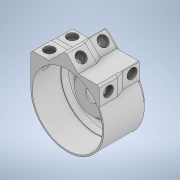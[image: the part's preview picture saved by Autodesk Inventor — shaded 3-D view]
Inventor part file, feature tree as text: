
AUTODESK INVENTOR PART (.ipt)
format: ipt  version: 2021 (Build 250183000, 183)  size: 588,288 bytes
history: native  units: mm
features: sketch x22, extrude x14, projected_geometry x9, hole x7, chamfer x6, fillet x2, plane x2, pattern_circular x2, other x2, revolve x1, loft x1
ambient origin geometry x8: Origin, YZ Plane, XZ Plane, XY Plane, X Axis, Y Axis, Z Axis, Center Point
bodies: Solid1 (feature_tree)
feature tree (68):
  extrude  "Extrusion1"  Depth=115.0mm TaperAngle=0.0deg
  extrude  "Extrusion2"  Depth=41.2mm TaperAngle=0.0deg
  extrude  "Extrusion3"  Depth=33.2mm TaperAngle=0.0deg
  revolve  "Revolution1"  [1 undecoded]
  extrude  "Extrusion4"  Depth=2.0mm
  fillet  "Fillet1"  Radius=2.0mm
  fillet  "Fillet2"  Radius=3.0mm
  hole  "Hole1"  [1 undecoded]
  plane  "Work Plane4"
  extrude  "Extrusion16"  Depth=26.0mm
  chamfer  "Chamfer1"  [1 undecoded]
  pattern_circular  "Circular Pattern1"  Count=8 Angle=360.0deg
  sketch  "Sketch8"  dims[d18=90.0deg d19=26.0mm d20=0.0mm d21=0.0mm]
  extrude  "Extrusion5"  Depth=38.0mm
  plane  "Work Plane1"
  extrude  "Extrusion6"  TaperAngle=0.0deg  [1 undecoded]
  pattern_circular  "Circular Pattern2"  Count=3 Angle=90.0deg
  extrude  "Extrusion7"  Depth=10.0mm
  extrude  "Extrusion8"  Depth=19.0mm
  extrude  "Extrusion9"  Depth=33.2mm TaperAngle=0.0deg
  extrude  "Extrusion10"  Depth=10.0mm TaperAngle=0.0deg
  extrude  "Extrusion11"  Depth=10.0mm TaperAngle=0.0deg
  extrude  "Extrusion12"  Depth=10.0mm TaperAngle=0.0deg
  hole  "Hole4"  [1 undecoded]
  hole  "Hole5"  [1 undecoded]
  hole  "Hole6"  [1 undecoded]
  hole  "Hole7"  [1 undecoded]
  hole  "Hole8"  [1 undecoded]
  hole  "Hole9"  [1 undecoded]
  extrude  "Extrusion15"  Depth=10.0mm TaperAngle=45.0deg
  chamfer  "Chamfer3"  Distance=25.0mm
  chamfer  "Chamfer4"  [1 undecoded]
  chamfer  "Chamfer5"  Distance=9.4mm
  chamfer  "Chamfer6"  Distance=10.0mm
  chamfer  "Chamfer7"  Angle=90.0deg  [1 undecoded]
  loft  "Loft1"
  sketch  "Sketch2"  dims[d0=150.0mm d1=115.0mm d2=0.0mm]
  sketch  "Sketch3"  dims[d3=70.4mm d4=41.2mm d5=0.0mm]
  sketch  "Sketch4"  dims[d6=86.4mm d7=33.2mm d8=0.0mm]
  sketch  "Sketch5"  dims[d9=10.0mm d10=2.0mm]
  sketch  "Sketch6"  dims[d11=2.0mm d12=2.0mm d13=2.0mm d14=3.0mm]
  sketch  "Sketch7"  dims[d16=4.886922mm d17=20.0mm]
  sketch  "Sketch9"  dims[d22=10.0mm]
  sketch  "Sketch10"  dims[d23=2.0mm]
  projected_geometry  "Projected Loop1"
  projected_geometry  "Projected Loop2"
  sketch  "Sketch11"  dims[d24=112.0mm]
  projected_geometry  "Projected Loop3"
  sketch  "Sketch12"  dims[d25=4.2mm d26=8.0mm d27=4.0mm d28=2.0mm d29=90.0deg d30=8.5mm d31=0.0mm]
  projected_geometry  "Projected Loop4"
  sketch  "Sketch13"  dims[d32=0.5mm d33=2.0mm d34=45.0deg d35=80.0mm d36=360.0deg]
  projected_geometry  "Projected Loop5"
  sketch  "Sketch14"  dims[d38=38.0mm d39=38.0mm]
  projected_geometry  "Projected Loop6"
  sketch  "Sketch15"  dims[d40=10.0mm d41=0.0mm d42=0.0mm]
  projected_geometry  "Projected Loop7"
  sketch  "Sketch24"  dims[d43=21.0mm]
  sketch  "Sketch25"  dims[d44=38.0mm]
  other  "Edges1"
  other  "Edges2"
  sketch  "Sketch27"  dims[d45=38.0mm]
  sketch  "Sketch28"  dims[d46=33.2mm d47=0.0mm d48=30.0mm d49=90.0deg]
  sketch  "Sketch29"  dims[d51=10.0mm d53=12.5mm]
  sketch  "Sketch30"  dims[d54=21.0mm d55=19.0mm]
  sketch  "Sketch31"  dims[d56=19.0mm d57=33.2mm d58=0.0mm]
  sketch  "Sketch32"  dims[d59=33.2mm d60=0.0mm d61=33.2mm d62=0.0mm d63=33.2mm d64=0.0mm d65=33.2mm d66=0.0mm d67=0.0mm d68=0.0mm d144=33.2mm d145=0.0mm d146=8.0mm d147=2.0mm d148=45.0deg d149=10.0mm d150=2.0mm d151=45.0deg d152=5.0mm d153=2.0mm d154=45.0deg d155=1.0mm d156=2.0mm d157=45.0deg d158=4.0mm d159=2.0mm d160=45.0deg d161=25.0mm d162=-5.0mm d163=9.4mm d164=10.0mm d165=0.0mm d166=0.0mm d167=90.0deg d168=0.0mm d169=90.0deg d170=1.0mm d171=45.0mm d172=11.5mm d180=20.752mm d181=10.0mm d182=4.0mm d183=2.0mm d184=90.0deg d185=61.1mm d186=20.594885mm d187=20.752mm d188=10.0mm d189=4.0mm d190=2.0mm d191=90.0deg d192=61.1mm d193=20.594885mm d194=20.752mm d195=10.0mm d196=4.0mm d197=2.0mm d198=90.0deg d199=61.1mm d200=20.594885mm d201=20.752mm d202=10.0mm d203=4.0mm d204=2.0mm d205=90.0deg d206=61.1mm d207=20.594885mm d208=20.752mm d209=10.0mm d210=4.0mm d211=2.0mm d212=90.0deg d213=61.1mm d214=20.594885mm d215=20.752mm d216=10.0mm d217=4.0mm d218=2.0mm d219=90.0deg d220=61.1mm d221=20.594885mm]
  projected_geometry  "Project Cut Edges1"
  projected_geometry  "Project Cut Edges2"
note: 12 required parameter values undecoded (feature->parameter linkage not recoverable at this tier; creation-order binding heuristic only, values carry confidence <= 0.55)